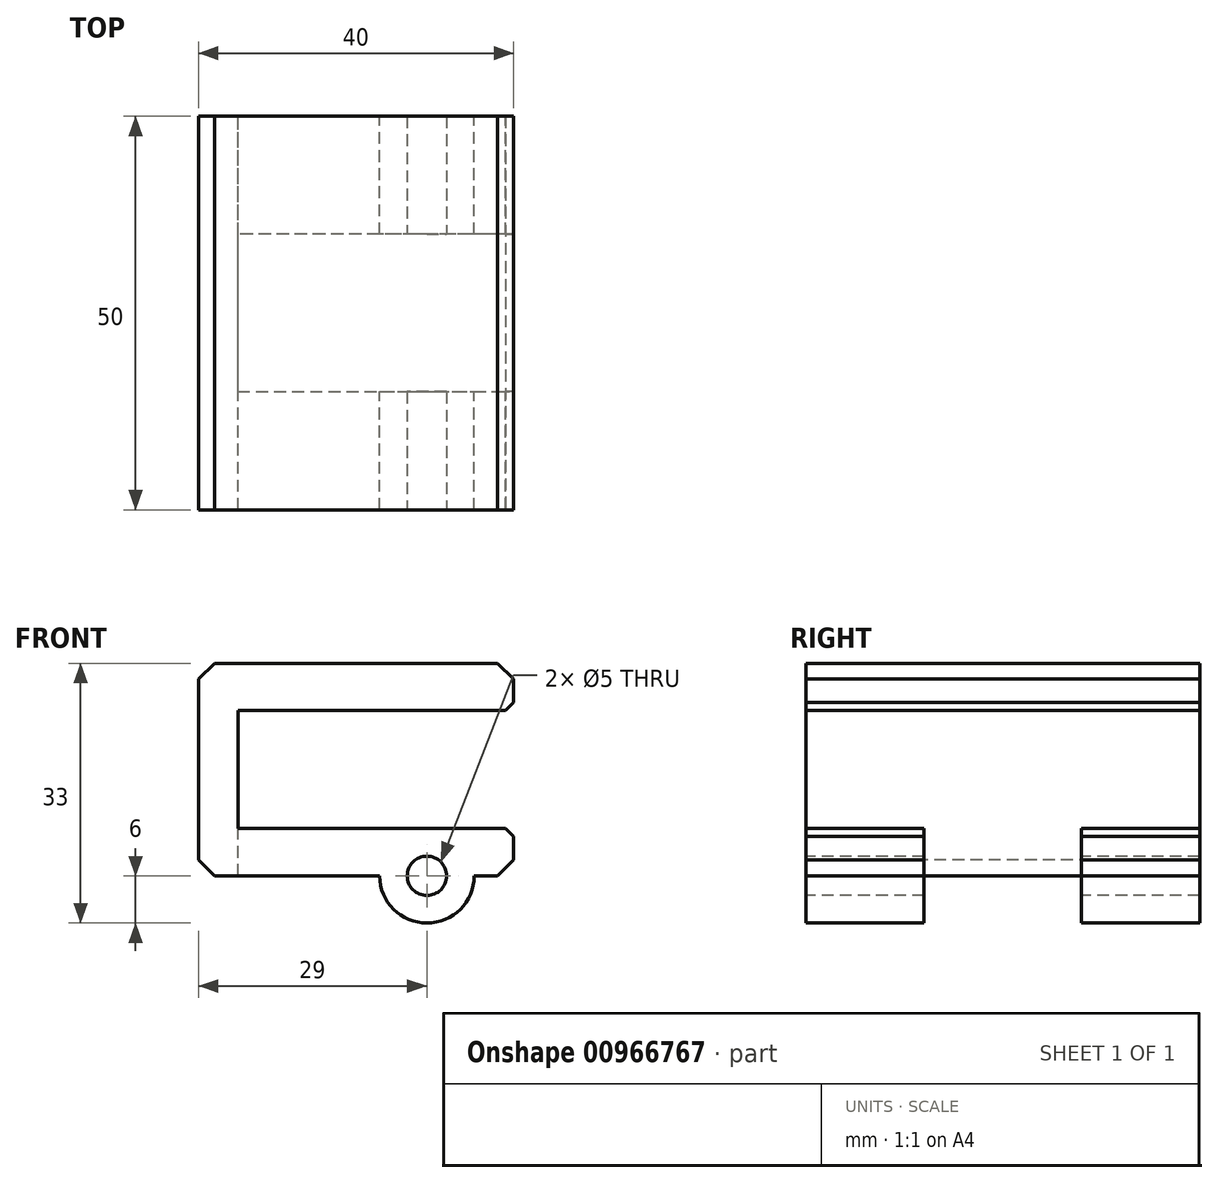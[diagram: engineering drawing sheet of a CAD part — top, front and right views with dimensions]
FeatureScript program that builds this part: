
annotation { "Feature Type Name" : "Feature", "Feature Type Description" : "" }
export const myFeature = defineFeature(function(context is Context, id is Id, definition is map)
    precondition{}
    {
        {
            var Q0;
            Q0=qCreatedBy(makeId("Front.planeOp"),FACE);
            var sketch = newSketch(context, id + "F0", { "sketchPlane" : qUnion([Q0])});
            skLineSegment(sketch, "E0", {"start": v(0, 0) * mm, "end": v(40, 0) * mm});
            skLineSegment(sketch, "E1", {"start": v(40, 0) * mm, "end": v(40, 6) * mm});
            skLineSegment(sketch, "E2", {"start": v(40, 6) * mm, "end": v(5, 6) * mm});
            skLineSegment(sketch, "E3", {"start": v(5, 6) * mm, "end": v(5, 21) * mm});
            skLineSegment(sketch, "E4", {"start": v(5, 21) * mm, "end": v(40, 21) * mm});
            skLineSegment(sketch, "E5", {"start": v(40, 21) * mm, "end": v(40, 27) * mm});
            skLineSegment(sketch, "E6", {"start": v(40, 27) * mm, "end": v(0, 27) * mm});
            skLineSegment(sketch, "E7", {"start": v(0, 27) * mm, "end": v(0, 0) * mm});
            skLineSegment(sketch, "E8", {"start": v(20, 0) * mm, "end": v(35, 0) * mm});
            skLineSegment(sketch, "E9", {"start": v(35, 0) * mm, "end": v(23, 0) * mm});
            skLineSegment(sketch, "E10", {"start": v(23, 0) * mm, "end": v(23, -6) * mm});
            skLineSegment(sketch, "E11", {"start": v(23, -6) * mm, "end": v(35, -6) * mm});
            skLineSegment(sketch, "E12", {"start": v(35, -6) * mm, "end": v(35, 0) * mm});
            skSolve(sketch);
        }
        {
            var Q0;
            {var subQ6=sQuery(id+"F0.wireOp",EDGE,"E1");Q0=makeQuery(id+"F0.imprint","IMPRINT",FACE,{"disambiguationData":[TD([[makeQuery(id+"F0.imprint","IMPRINT",EDGE,{"derivedFrom":subQ6}),1.0]])]});}
            var Q1;
            {var subQ0=sQuery(id+"F0.wireOp",EDGE,"E10");Q1=makeQuery(id+"F0.imprint","IMPRINT",FACE,{"disambiguationData":[TD([[makeQuery(id+"F0.imprint","IMPRINT",EDGE,{"derivedFrom":subQ0}),1.0]])]});}
            extrude(context, id + "F1", {"entities" : qUnion([Q0, Q1]), "depth" : 50 * mm, "offsetDistance" : 25 * mm});
        }
        {
            var Q0;
            Q0=makeQuery(id+"F1.opExtrude","SWEPT_EDGE",EDGE,{"disambiguationData":[OSD([sQuery(id+"F0.wireOp",EDGE,"E10"),sQuery(id+"F0.wireOp",EDGE,"E11")])]});
            var Q1;
            Q1=makeQuery(id+"F1.opExtrude","SWEPT_EDGE",EDGE,{"disambiguationData":[OSD([sQuery(id+"F0.wireOp",EDGE,"E11"),sQuery(id+"F0.wireOp",EDGE,"E12")])]});
            fillet(context, id + "F2", {"entities" : qUnion([Q0, Q1]), "radius" : 6 * mm, "tangentPropagation" : true, "allowEdgeOverflow" : false});
        }
        {
            var Q0;
            Q0=makeQuery(id+"F1.opExtrude","SWEPT_FACE",FACE,{"disambiguationData":[OSD([sQuery(id+"F0.wireOp",EDGE,"E2")])]});
            var sketch = newSketch(context, id + "F3", { "sketchPlane" : qUnion([Q0])});
            skLineSegment(sketch, "E13", {"start": v(40, -25) * mm, "end": v(40, -15) * mm});
            skLineSegment(sketch, "E14", {"start": v(40, -15) * mm, "end": v(5, -15) * mm});
            skLineSegment(sketch, "E15", {"start": v(5, -15) * mm, "end": v(5, -35) * mm});
            skLineSegment(sketch, "E16", {"start": v(5, -35) * mm, "end": v(40, -35) * mm});
            skLineSegment(sketch, "E17", {"start": v(40, -35) * mm, "end": v(40, -25) * mm});
            skSolve(sketch);
        }
        {
            var Q0;
            Q0 = qSketchRegion(id + "F3", true);
            extrude(context, id + "F4", {"entities" : qUnion([Q0]), "operationType" : NewBodyOperationType.REMOVE, "oppositeDirection" : true, "depth" : 25 * mm, "offsetDistance" : 25 * mm});
        }
        {
            var Q0;
            Q0=makeQuery(id+"F1.opExtrude","CAP_FACE",FACE,{"disambiguationData":[OSD([sQuery(id+"F0.wireOp",EDGE,"E0"),sQuery(id+"F0.wireOp",EDGE,"E1"),sQuery(id+"F0.wireOp",EDGE,"E2"),sQuery(id+"F0.wireOp",EDGE,"E3"),sQuery(id+"F0.wireOp",EDGE,"E4"),sQuery(id+"F0.wireOp",EDGE,"E5"),sQuery(id+"F0.wireOp",EDGE,"E6"),sQuery(id+"F0.wireOp",EDGE,"E7"),sQuery(id+"F0.wireOp",EDGE,"E8"),sQuery(id+"F0.wireOp",EDGE,"E10"),sQuery(id+"F0.wireOp",EDGE,"E11"),sQuery(id+"F0.wireOp",EDGE,"E12")])],"isStart":false});
            var sketch = newSketch(context, id + "F5", { "sketchPlane" : qUnion([Q0])});
            skLineSegment(sketch, "E18", {"start": v(29, -6) * mm, "end": v(29, 0) * mm});
            skCircle(sketch, "E19", {"center": v(29, 0) * mm, "radius": 2.5 * mm});
            skSolve(sketch);
        }
        {
            var Q0;
            Q0 = qSketchRegion(id + "F5", true);
            extrude(context, id + "F6", {"entities" : qUnion([Q0]), "operationType" : NewBodyOperationType.REMOVE, "oppositeDirection" : true, "depth" : 60 * mm, "offsetDistance" : 25 * mm});
        }
        {
            var Q0;
            Q0=makeQuery(id+"F1.opExtrude","SWEPT_EDGE",EDGE,{"disambiguationData":[OSD([sQuery(id+"F0.wireOp",EDGE,"E6"),sQuery(id+"F0.wireOp",EDGE,"E7")])]});
            var Q1;
            Q1=makeQuery(id+"F1.opExtrude","SWEPT_EDGE",EDGE,{"disambiguationData":[OSD([sQuery(id+"F0.wireOp",EDGE,"E5"),sQuery(id+"F0.wireOp",EDGE,"E6")])]});
            var Q2;
            Q2=makeQuery(id+"F1.opExtrude","SWEPT_EDGE",EDGE,{"disambiguationData":[OSD([sQuery(id+"F0.wireOp",EDGE,"E0"),sQuery(id+"F0.wireOp",EDGE,"E7")])]});
            var Q3;
            {var subQ0=sQuery(id+"F0.wireOp",EDGE,"E1");var subQ1=sQuery(id+"F0.wireOp",EDGE,"E0");Q3=makeQuery(id+"F4.boolean.opBoolean","SPLIT",EDGE,{"disambiguationData":[TD([makeQuery(id+"F4.opExtrude","SWEPT_FACE",FACE,{"disambiguationData":[OSD([sQuery(id+"F3.wireOp",EDGE,"E16")])]})])],"derivedFrom":makeQuery(id+"F1.opExtrude","SWEPT_EDGE",EDGE,{"disambiguationData":[OSD([subQ1,subQ0])]})});}
            var Q4;
            {var subQ0=sQuery(id+"F0.wireOp",EDGE,"E1");var subQ1=sQuery(id+"F0.wireOp",EDGE,"E0");Q4=makeQuery(id+"F4.boolean.opBoolean","SPLIT",EDGE,{"disambiguationData":[TD([makeQuery(id+"F4.opExtrude","SWEPT_FACE",FACE,{"disambiguationData":[OSD([sQuery(id+"F3.wireOp",EDGE,"E14")])]})])],"derivedFrom":makeQuery(id+"F1.opExtrude","SWEPT_EDGE",EDGE,{"disambiguationData":[OSD([subQ1,subQ0])]})});}
            chamfer(context, id + "F7", {"entities" : qUnion([Q0, Q1, Q2, Q3, Q4]), "width" : 2 * mm, "tangentPropagation" : true});
        }
        {
            var Q0;
            {var subQ0=sQuery(id+"F0.wireOp",EDGE,"E2");var subQ1=sQuery(id+"F0.wireOp",EDGE,"E1");Q0=makeQuery(id+"F4.boolean.opBoolean","SPLIT",EDGE,{"disambiguationData":[TD([makeQuery(id+"F4.opExtrude","SWEPT_FACE",FACE,{"disambiguationData":[OSD([sQuery(id+"F3.wireOp",EDGE,"E16")])]})])],"derivedFrom":makeQuery(id+"F1.opExtrude","SWEPT_EDGE",EDGE,{"disambiguationData":[OSD([subQ1,subQ0])]})});}
            var Q1;
            {var subQ0=sQuery(id+"F0.wireOp",EDGE,"E2");var subQ1=sQuery(id+"F0.wireOp",EDGE,"E1");Q1=makeQuery(id+"F4.boolean.opBoolean","SPLIT",EDGE,{"disambiguationData":[TD([makeQuery(id+"F4.opExtrude","SWEPT_FACE",FACE,{"disambiguationData":[OSD([sQuery(id+"F3.wireOp",EDGE,"E14")])]})])],"derivedFrom":makeQuery(id+"F1.opExtrude","SWEPT_EDGE",EDGE,{"disambiguationData":[OSD([subQ1,subQ0])]})});}
            var Q2;
            Q2=makeQuery(id+"F1.opExtrude","SWEPT_EDGE",EDGE,{"disambiguationData":[OSD([sQuery(id+"F0.wireOp",EDGE,"E4"),sQuery(id+"F0.wireOp",EDGE,"E5")])]});
            chamfer(context, id + "F8", {"entities" : qUnion([Q0, Q1, Q2]), "width" : 1 * mm, "tangentPropagation" : true});
        }
    });
